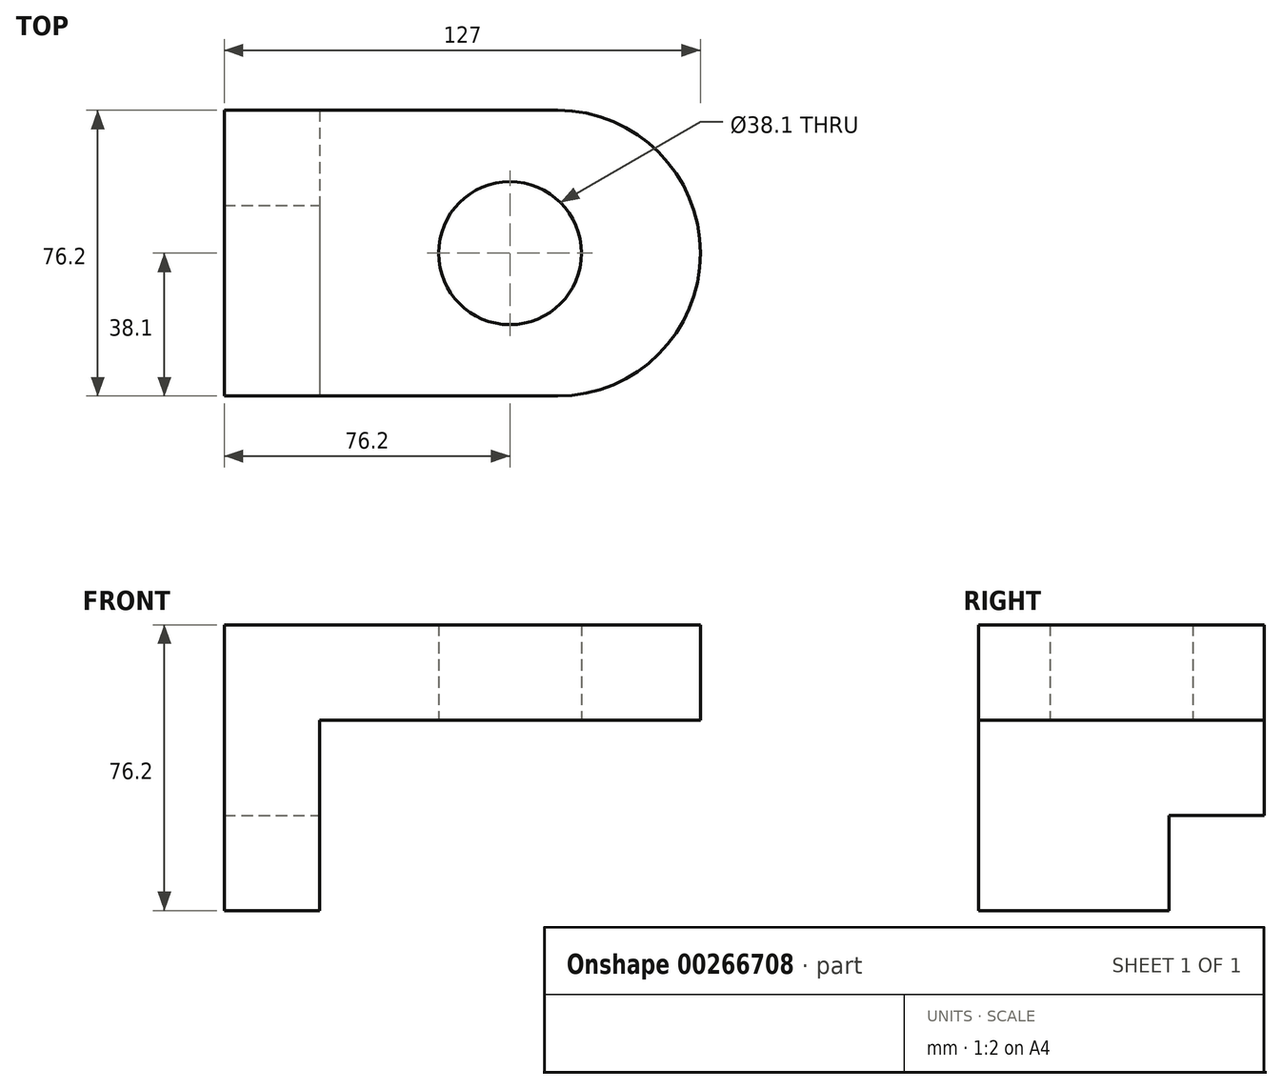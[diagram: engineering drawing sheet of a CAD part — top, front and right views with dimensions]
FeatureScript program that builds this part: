
annotation { "Feature Type Name" : "Feature", "Feature Type Description" : "" }
export const myFeature = defineFeature(function(context is Context, id is Id, definition is map)
    precondition{}
    {
        {
            var Q0;
            Q0=qCreatedBy(makeId("Top.planeOp"),FACE);
            var sketch = newSketch(context, id + "F0", { "sketchPlane" : qUnion([Q0])});
            skLineSegment(sketch, "E0.bottom", {"start": v(-50.8, 38.1) * mm, "end": v(50.8, 38.1) * mm});
            skLineSegment(sketch, "E0.top", {"start": v(-50.8, -38.1) * mm, "end": v(50.8, -38.1) * mm});
            skLineSegment(sketch, "E0.left", {"start": v(-50.8, 38.1) * mm, "end": v(-50.8, -38.1) * mm});
            skLineSegment(sketch, "E0.right", {"start": v(50.8, 38.1) * mm, "end": v(50.8, -38.1) * mm});
            skPoint(sketch, "E0.middle", {"position": v(0, 0) * mm});
            skSolve(sketch);
        }
        {
            var Q0;
            Q0 = qSketchRegion(id + "F0", true);
            extrude(context, id + "F1", {"entities" : qUnion([Q0]), "depth" : 25.4 * mm});
        }
        {
            var Q0;
            Q0=makeQuery(id+"F1.opExtrude","SWEPT_EDGE",EDGE,{"disambiguationData":[OSD([sQuery(id+"F0.wireOp",EDGE,"E0.top"),sQuery(id+"F0.wireOp",EDGE,"E0.right")])]});
            var Q1;
            Q1=makeQuery(id+"F1.opExtrude","SWEPT_EDGE",EDGE,{"disambiguationData":[OSD([sQuery(id+"F0.wireOp",EDGE,"E0.bottom"),sQuery(id+"F0.wireOp",EDGE,"E0.right")])]});
            fillet(context, id + "F2", {"entities" : qUnion([Q0, Q1]), "radius" : 38.1 * mm, "tangentPropagation" : true, "allowEdgeOverflow" : false});
        }
        {
            var Q0;
            Q0=qCreatedBy(makeId("Top.planeOp"),FACE);
            var sketch = newSketch(context, id + "F3", { "sketchPlane" : qUnion([Q0])});
            skCircle(sketch, "E1", {"center": v(0, 0) * mm, "radius": 19.05 * mm});
            skSolve(sketch);
        }
        {
            var Q0;
            Q0 = qSketchRegion(id + "F3", true);
            extrude(context, id + "F4", {"entities" : qUnion([Q0]), "operationType" : NewBodyOperationType.REMOVE, "endBound" : BoundingType.THROUGH_ALL, "depth" : 25.4 * mm});
        }
        {
            var Q0;
            Q0=makeQuery(id+"F1.opExtrude","CAP_FACE",FACE,{"disambiguationData":[OSD([sQuery(id+"F0.wireOp",EDGE,"E0.bottom"),sQuery(id+"F0.wireOp",EDGE,"E0.top"),sQuery(id+"F0.wireOp",EDGE,"E0.left"),sQuery(id+"F0.wireOp",EDGE,"E0.right")])],"isStart":false});
            var sketch = newSketch(context, id + "F5", { "sketchPlane" : qUnion([Q0])});
            skPoint(sketch, "E2.oppositeSnap0", {"position": v(-19.05, -38.1) * mm});
            skLineSegment(sketch, "E2.bottom", {"start": v(-50.8, 38.1) * mm, "end": v(-76.2, 38.1) * mm});
            skLineSegment(sketch, "E2.top", {"start": v(-50.8, -38.1) * mm, "end": v(-76.2, -38.1) * mm});
            skLineSegment(sketch, "E2.left", {"start": v(-50.8, 38.1) * mm, "end": v(-50.8, -38.1) * mm});
            skLineSegment(sketch, "E2.right", {"start": v(-76.2, 38.1) * mm, "end": v(-76.2, -38.1) * mm});
            skSolve(sketch);
        }
        {
            var Q0;
            Q0 = qSketchRegion(id + "F5", true);
            extrude(context, id + "F6", {"entities" : qUnion([Q0]), "operationType" : NewBodyOperationType.ADD, "oppositeDirection" : true, "depth" : 76.2 * mm});
        }
        {
            var Q0;
            Q0=makeQuery(id+"F6.opExtrude","SWEPT_FACE",FACE,{"disambiguationData":[OSD([sQuery(id+"F5.wireOp",EDGE,"E2.left")])]});
            var sketch = newSketch(context, id + "F7", { "sketchPlane" : qUnion([Q0])});
            skLineSegment(sketch, "E3.bottom", {"start": v(38.1, -50.8) * mm, "end": v(12.7, -50.8) * mm});
            skLineSegment(sketch, "E3.top", {"start": v(38.1, -25.4) * mm, "end": v(12.7, -25.4) * mm});
            skLineSegment(sketch, "E3.left", {"start": v(38.1, -50.8) * mm, "end": v(38.1, -25.4) * mm});
            skLineSegment(sketch, "E3.right", {"start": v(12.7, -50.8) * mm, "end": v(12.7, -25.4) * mm});
            skSolve(sketch);
        }
        {
            var Q0;
            Q0=makeQuery(id+"F7.imprint","IMPRINT",FACE,{"disambiguationData":[TD([[makeQuery(id+"F7.imprint","IMPRINT",EDGE,{"derivedFrom":sQuery(id+"F7.wireOp",EDGE,"E3.bottom")}),-1.0]])]});
            extrude(context, id + "F8", {"entities" : qUnion([Q0]), "operationType" : NewBodyOperationType.REMOVE, "oppositeDirection" : true, "depth" : 25.4 * mm});
        }
    });
